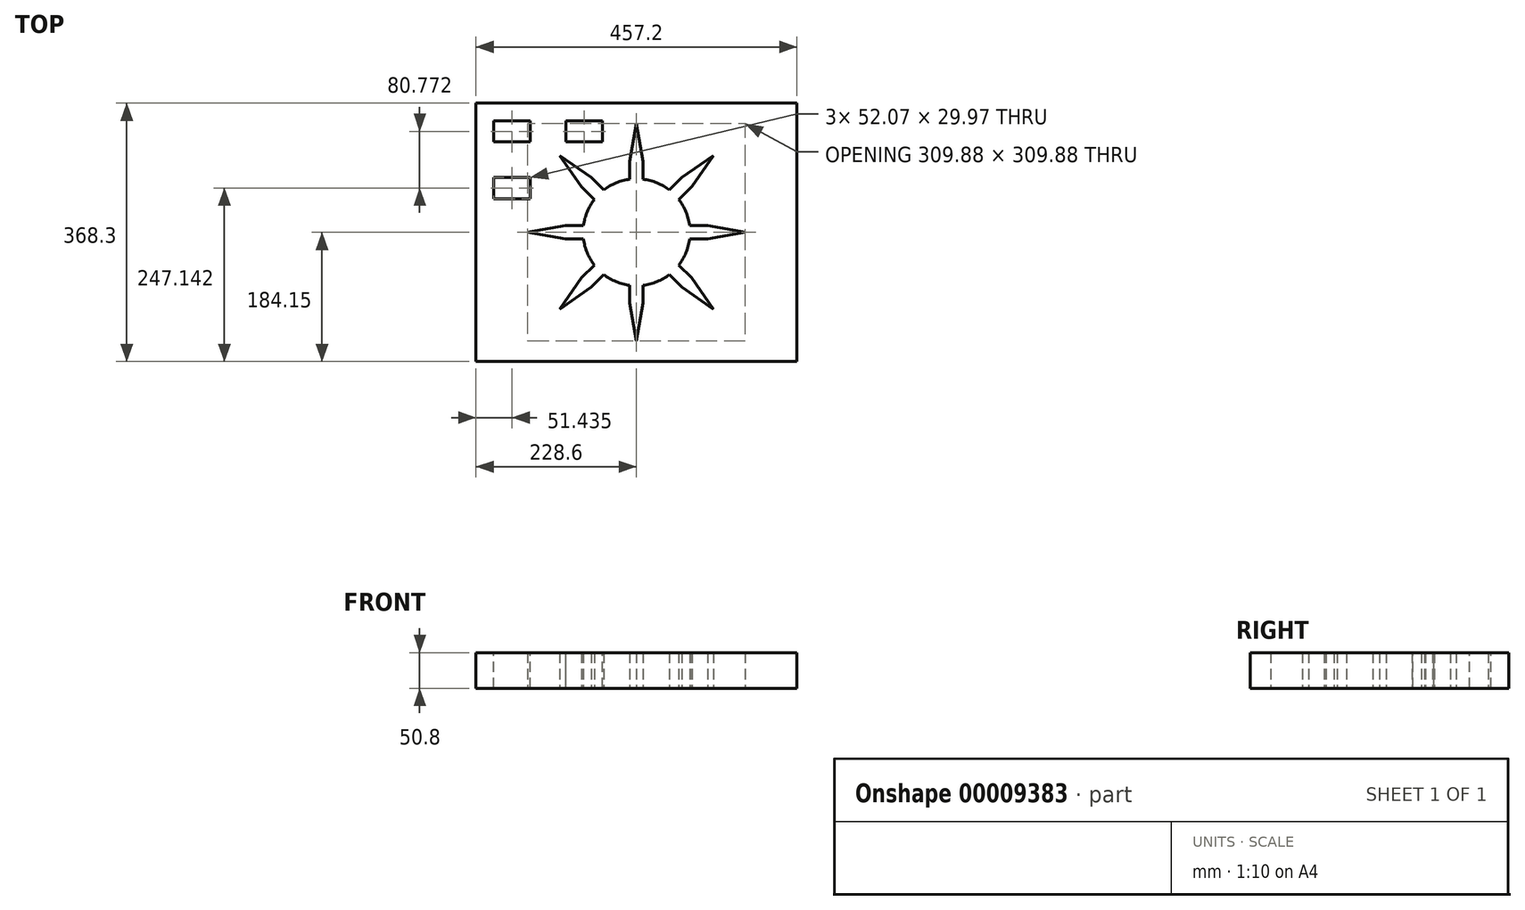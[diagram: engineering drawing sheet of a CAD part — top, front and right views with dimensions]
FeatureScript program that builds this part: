
annotation { "Feature Type Name" : "Feature", "Feature Type Description" : "" }
export const myFeature = defineFeature(function(context is Context, id is Id, definition is map)
    precondition{}
    {
        {
            var Q0;
            Q0=qCreatedBy(makeId("Top.planeOp"),FACE);
            var sketch = newSketch(context, id + "F0", { "sketchPlane" : qUnion([Q0])});
            skLineSegment(sketch, "E0.rect.bottom", {"start": v(-228.6, 184.15) * mm, "end": v(228.6, 184.15) * mm});
            skLineSegment(sketch, "E0.rect.top", {"start": v(-228.6, -184.15) * mm, "end": v(228.6, -184.15) * mm});
            skLineSegment(sketch, "E0.rect.left", {"start": v(-228.6, 184.15) * mm, "end": v(-228.6, -184.15) * mm});
            skLineSegment(sketch, "E0.rect.right", {"start": v(228.6, 184.15) * mm, "end": v(228.6, -184.15) * mm});
            skPoint(sketch, "E0.rect.middle", {"position": v(0, 0) * mm});
            skCircle(sketch, "E1", {"center": v(0, 0) * mm, "radius": 76.2 * mm});
            skLineSegment(sketch, "E2", {"start": v(-9.53, 75.6) * mm, "end": v(-9.53, 101) * mm});
            skLineSegment(sketch, "E3", {"start": v(-9.53, 101) * mm, "end": v(0, 154.94) * mm});
            skLineSegment(sketch, "E4", {"start": v(9.52, 75.6) * mm, "end": v(9.52, 101) * mm});
            skLineSegment(sketch, "E5", {"start": v(9.52, 101) * mm, "end": v(0, 154.94) * mm});
            skLineSegment(sketch, "E6", {"start": v(-9.53, -75.6) * mm, "end": v(-9.53, -101) * mm});
            skLineSegment(sketch, "E7", {"start": v(-9.53, -101) * mm, "end": v(0, -154.94) * mm});
            skLineSegment(sketch, "E8", {"start": v(9.52, -75.6) * mm, "end": v(9.52, -101) * mm});
            skLineSegment(sketch, "E9", {"start": v(9.52, -101) * mm, "end": v(0, -154.94) * mm});
            skLineSegment(sketch, "E10", {"start": v(-101, 9.52) * mm, "end": v(-75.6, 9.52) * mm});
            skLineSegment(sketch, "E11", {"start": v(-101, -9.53) * mm, "end": v(-75.6, -9.52) * mm});
            skLineSegment(sketch, "E12", {"start": v(154.94, 0) * mm, "end": v(101, -9.52) * mm});
            skLineSegment(sketch, "E13", {"start": v(101, -9.52) * mm, "end": v(75.6, -9.52) * mm});
            skLineSegment(sketch, "E14", {"start": v(154.94, 0) * mm, "end": v(101, 9.53) * mm});
            skLineSegment(sketch, "E15", {"start": v(101, 9.53) * mm, "end": v(75.6, 9.52) * mm});
            skLineSegment(sketch, "E16", {"start": v(0, 0) * mm, "end": v(-154.94, 0) * mm});
            skLineSegment(sketch, "E17", {"start": v(-154.94, 0) * mm, "end": v(-101, 9.53) * mm});
            skLineSegment(sketch, "E18", {"start": v(-101, -9.53) * mm, "end": v(-154.94, 0) * mm});
            skLineSegment(sketch, "E19", {"start": v(0, 0) * mm, "end": v(154.94, 0) * mm});
            skLineSegment(sketch, "E20", {"start": v(60.2, 46.72) * mm, "end": v(79.16, 65.7) * mm});
            skLineSegment(sketch, "E21", {"start": v(46.72, 60.2) * mm, "end": v(64.56, 78.03) * mm});
            skLineSegment(sketch, "E22", {"start": v(64.56, 78.03) * mm, "end": v(109.56, 109.56) * mm});
            skLineSegment(sketch, "E23", {"start": v(109.56, 109.56) * mm, "end": v(79.16, 65.7) * mm});
            skLineSegment(sketch, "E24", {"start": v(-46.72, 60.2) * mm, "end": v(-64.68, 78.15) * mm});
            skLineSegment(sketch, "E25", {"start": v(-60.2, 46.72) * mm, "end": v(-78.15, 64.68) * mm});
            skLineSegment(sketch, "E26", {"start": v(-64.68, 78.15) * mm, "end": v(-109.56, 109.56) * mm});
            skLineSegment(sketch, "E27", {"start": v(-109.56, 109.56) * mm, "end": v(-78.15, 64.68) * mm});
            skLineSegment(sketch, "E28", {"start": v(-60.2, -46.72) * mm, "end": v(-78.15, -64.68) * mm});
            skLineSegment(sketch, "E29", {"start": v(-46.72, -60.2) * mm, "end": v(-64.68, -78.15) * mm});
            skLineSegment(sketch, "E30", {"start": v(-78.15, -64.68) * mm, "end": v(-109.56, -109.56) * mm});
            skLineSegment(sketch, "E31", {"start": v(-109.56, -109.56) * mm, "end": v(-64.68, -78.15) * mm});
            skLineSegment(sketch, "E32", {"start": v(46.72, -60.2) * mm, "end": v(64.68, -78.15) * mm});
            skLineSegment(sketch, "E33", {"start": v(60.2, -46.72) * mm, "end": v(78.15, -64.68) * mm});
            skLineSegment(sketch, "E34", {"start": v(78.15, -64.68) * mm, "end": v(109.56, -109.56) * mm});
            skLineSegment(sketch, "E35", {"start": v(109.56, -109.56) * mm, "end": v(64.68, -78.15) * mm});
            skLineSegment(sketch, "E36", {"start": v(-109.56, 109.56) * mm, "end": v(0, 0) * mm});
            skLineSegment(sketch, "E37", {"start": v(0, 0) * mm, "end": v(109.56, -109.56) * mm});
            skLineSegment(sketch, "E38", {"start": v(0, 0) * mm, "end": v(109.56, 109.56) * mm});
            skLineSegment(sketch, "E39", {"start": v(0, 0) * mm, "end": v(-109.56, -109.56) * mm});
            skLineSegment(sketch, "E40", {"start": v(0, 0) * mm, "end": v(0, -154.94) * mm});
            skLineSegment(sketch, "E41", {"start": v(0, 154.94) * mm, "end": v(0, 0) * mm});
            skSolve(sketch);
        }
        {
            var Q0;
            Q0=makeQuery(id+"F0.imprint","IMPRINT",FACE,{"disambiguationData":[TD([[makeQuery(id+"F0.imprint","IMPRINT",EDGE,{"derivedFrom":sQuery(id+"F0.wireOp",EDGE,"E0.rect.bottom")}),-1.0]])]});
            extrude(context, id + "F1", {"entities" : qUnion([Q0]), "depth" : 50.8 * mm});
        }
        {
            var Q0;
            Q0=makeQuery(id+"F1.opExtrude","CAP_FACE",FACE,{"disambiguationData":[OSD([sQuery(id+"F0.wireOp",EDGE,"E0.rect.bottom"),sQuery(id+"F0.wireOp",EDGE,"E0.rect.top"),sQuery(id+"F0.wireOp",EDGE,"E0.rect.left"),sQuery(id+"F0.wireOp",EDGE,"E0.rect.right"),sQuery(id+"F0.wireOp",EDGE,"E1"),sQuery(id+"F0.wireOp",EDGE,"E2"),sQuery(id+"F0.wireOp",EDGE,"E3"),sQuery(id+"F0.wireOp",EDGE,"E4"),sQuery(id+"F0.wireOp",EDGE,"E5"),sQuery(id+"F0.wireOp",EDGE,"E6"),sQuery(id+"F0.wireOp",EDGE,"E7"),sQuery(id+"F0.wireOp",EDGE,"E8"),sQuery(id+"F0.wireOp",EDGE,"E9"),sQuery(id+"F0.wireOp",EDGE,"E10"),sQuery(id+"F0.wireOp",EDGE,"E11"),sQuery(id+"F0.wireOp",EDGE,"E12"),sQuery(id+"F0.wireOp",EDGE,"E13"),sQuery(id+"F0.wireOp",EDGE,"E14"),sQuery(id+"F0.wireOp",EDGE,"E15"),sQuery(id+"F0.wireOp",EDGE,"E17"),sQuery(id+"F0.wireOp",EDGE,"E18"),sQuery(id+"F0.wireOp",EDGE,"E20"),sQuery(id+"F0.wireOp",EDGE,"E21"),sQuery(id+"F0.wireOp",EDGE,"E22"),sQuery(id+"F0.wireOp",EDGE,"E23"),sQuery(id+"F0.wireOp",EDGE,"E24"),sQuery(id+"F0.wireOp",EDGE,"E25"),sQuery(id+"F0.wireOp",EDGE,"E26"),sQuery(id+"F0.wireOp",EDGE,"E27"),sQuery(id+"F0.wireOp",EDGE,"E28"),sQuery(id+"F0.wireOp",EDGE,"E29"),sQuery(id+"F0.wireOp",EDGE,"E30"),sQuery(id+"F0.wireOp",EDGE,"E31"),sQuery(id+"F0.wireOp",EDGE,"E32"),sQuery(id+"F0.wireOp",EDGE,"E33"),sQuery(id+"F0.wireOp",EDGE,"E34"),sQuery(id+"F0.wireOp",EDGE,"E35")])],"isStart":false});
            var sketch = newSketch(context, id + "F2", { "sketchPlane" : qUnion([Q0])});
            skLineSegment(sketch, "E42.rect.bottom", {"start": v(-151.13, 128.78) * mm, "end": v(-203.2, 128.78) * mm});
            skLineSegment(sketch, "E42.rect.top", {"start": v(-151.13, 158.75) * mm, "end": v(-203.2, 158.75) * mm});
            skLineSegment(sketch, "E42.rect.left", {"start": v(-151.13, 128.78) * mm, "end": v(-151.13, 158.75) * mm});
            skLineSegment(sketch, "E42.rect.right", {"start": v(-203.2, 128.78) * mm, "end": v(-203.2, 158.75) * mm});
            skPoint(sketch, "E42.rect.middle", {"position": v(-177.16, 143.76) * mm});
            skLineSegment(sketch, "E43.rect.bottom", {"start": v(-151.13, 77.98) * mm, "end": v(-203.2, 77.98) * mm});
            skLineSegment(sketch, "E43.rect.top", {"start": v(-151.13, 48) * mm, "end": v(-203.2, 48) * mm});
            skLineSegment(sketch, "E43.rect.left", {"start": v(-151.13, 77.98) * mm, "end": v(-151.13, 48) * mm});
            skLineSegment(sketch, "E43.rect.right", {"start": v(-203.2, 77.98) * mm, "end": v(-203.2, 48) * mm});
            skPoint(sketch, "E43.rect.middle", {"position": v(-177.16, 63) * mm});
            skLineSegment(sketch, "E44.rect.bottom", {"start": v(-100.33, 128.78) * mm, "end": v(-48.26, 128.78) * mm});
            skLineSegment(sketch, "E44.rect.top", {"start": v(-100.33, 158.75) * mm, "end": v(-48.26, 158.75) * mm});
            skLineSegment(sketch, "E44.rect.left", {"start": v(-100.33, 128.78) * mm, "end": v(-100.33, 158.75) * mm});
            skLineSegment(sketch, "E44.rect.right", {"start": v(-48.26, 128.78) * mm, "end": v(-48.26, 158.75) * mm});
            skPoint(sketch, "E44.rect.middle", {"position": v(-74.3, 143.76) * mm});
            skSolve(sketch);
        }
        {
            var Q0;
            Q0=makeQuery(id+"F2.imprint","IMPRINT",FACE,{"disambiguationData":[TD([[makeQuery(id+"F2.imprint","IMPRINT",EDGE,{"derivedFrom":sQuery(id+"F2.wireOp",EDGE,"E42.rect.bottom")}),-1.0]])]});
            var Q1;
            Q1=makeQuery(id+"F2.imprint","IMPRINT",FACE,{"disambiguationData":[TD([[makeQuery(id+"F2.imprint","IMPRINT",EDGE,{"derivedFrom":sQuery(id+"F2.wireOp",EDGE,"E43.rect.bottom")}),1.0]])]});
            var Q2;
            Q2=makeQuery(id+"F2.imprint","IMPRINT",FACE,{"disambiguationData":[TD([[makeQuery(id+"F2.imprint","IMPRINT",EDGE,{"derivedFrom":sQuery(id+"F2.wireOp",EDGE,"E44.rect.bottom")}),1.0]])]});
            extrude(context, id + "F3", {"entities" : qUnion([Q0, Q1, Q2]), "operationType" : NewBodyOperationType.REMOVE, "oppositeDirection" : true, "depth" : 50.8 * mm});
        }
    });
